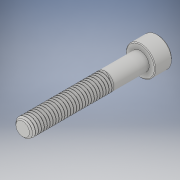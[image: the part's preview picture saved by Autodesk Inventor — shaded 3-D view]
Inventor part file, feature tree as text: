
AUTODESK INVENTOR PART (.ipt)
format: ipt  version: 2018 (Build 220112000, 112)  size: 936,960 bytes
history: native  units: in
note: dims shown in document units (in); Inventor stores cm internally (conversion verified against a paired STEP export)
features: chamfer x1
ambient origin geometry x8: Origin, YZ Plane, XZ Plane, XY Plane, X Axis, Y Axis, Z Axis, Center Point
bodies: Solid1 (feature_tree)
feature tree (1):
  chamfer  "Chamfer2"  [1 undecoded]
note: 1 required parameter value undecoded (feature->parameter linkage not recoverable at this tier; creation-order binding heuristic only, values carry confidence <= 0.55)
